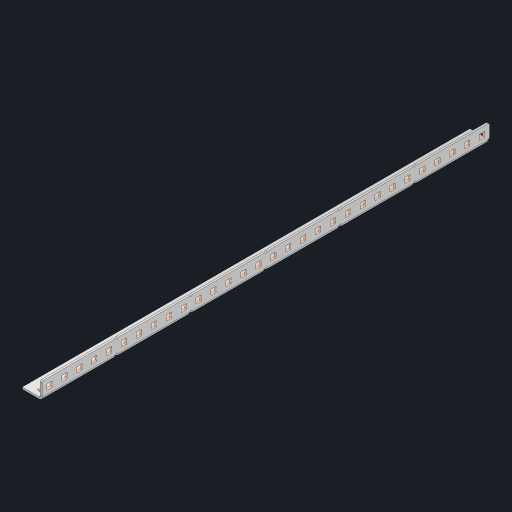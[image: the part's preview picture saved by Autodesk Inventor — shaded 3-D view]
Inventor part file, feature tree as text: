
AUTODESK INVENTOR PART (.ipt)
format: ipt  version: 2023 (Build 270158000, 158)  size: 974,848 bytes
history: native  units: in
note: dims shown in document units (in); Inventor stores cm internally (conversion verified against a paired STEP export)
features: other x65, extrude x59, sheet_metal_op x10, sketch x8, mirror x1, pattern_linear x1, chamfer x1
ambient origin geometry x8: Origin, YZ Plane, XZ Plane, XY Plane, X Axis, Y Axis, Z Axis, Center Point
bodies: Solid1 (feature_tree), Body (feature_tree)
feature tree (145):
  other  "Flange Pattern Plane"
  sheet_metal_op  "Flange Pattern"
  sheet_metal_op  "Body Pattern"
  other  "Arc Length"
  mirror  "Notch Mirror"
  pattern_linear  "Notch Pattern"  Spacing1=0.25in  [1 undecoded]
  chamfer  "End Chamfer"
  extrude  "Half Cut"  Depth=0.0625in
  sketch  "Sketch1"  dims[d0=1.5in]
  other  "Plate1"
  sketch  "Sketch2"  dims[d1=15.0in]
  other  "Plate2"
  sheet_metal_op  "Bend1"
  sheet_metal_op  "Corner1"
  sketch  "Sketch3"  dims[d2=0.0625in]
  other  "Flange Pattern Sketch"
  sketch  "Sketch7"  dims[d3=0.0625in]
  other  "Srf1"
  other  "Srf2"
  sketch  "Sketch8"  dims[d4=0.0312in]
  sketch  "Sketch9"  dims[d5=0.125in]
  other  "Srf91"
  sheet_metal_op  "Body Pattern Sketch"
  other  "Srf92"
  sketch  "Sketch13"  dims[d6=0.0625in]
  sketch  "Sketch14"  dims[d7=0.5in d8=90.0deg d9=0.0312in d10=0.25in d11=0.0625in d12=0.0625in d16=0.182in d17=0.02in d18=0.0625in d19=0.0in d20=0.25in d21=0.25in d46=0.172in d47=1.0in d48=0.0in d49=0.182in d50=0.02in d51=0.25in d52=0.25in d53=0.0625in d54=0.0in d55=0.172in d56=1.0in d57=0.0in d60=11.811in d62=0.5in d63=0.3937in d65=0.5in d85=0.1473in d86=0.1782in d88=0.04in d89=0.0625in d90=0.0in d91=0.04in d92=0.0491in d95=2.5in d96=0.04in d97=0.25in d98=45.0deg d101=0.0in d102=2.497in d131=0.5in d132=11.811in d134=0.5in d139=0.5in]
  other  "Srf856"
  other  "Srf1310"
  other  "Srf1311"
  other  "Srf1312"
  other  "Srf1376"
  other  "Srf1377"
  other  "Srf1728"
  other  "Srf1755"
  other  "Srf1878"
  other  "Srf1879"
  other  "Srf1880"
  other  "Srf1881"
  other  "Srf1882"
  other  "Srf1883"
  other  "Srf1884"
  other  "Srf1885"
  other  "Srf1886"
  other  "Srf1887"
  other  "Srf1888"
  other  "Srf1889"
  other  "Srf1890"
  other  "Srf1891"
  other  "Srf1892"
  other  "Srf1893"
  other  "Srf1894"
  other  "Srf1895"
  other  "Srf1896"
  other  "Srf1897"
  other  "Srf1898"
  other  "Srf1899"
  other  "Srf1900"
  other  "Srf1901"
  other  "Srf1942"
  other  "Srf1943"
  other  "Srf1944"
  other  "Srf1945"
  other  "Srf1946"
  other  "Srf1947"
  other  "Srf1948"
  other  "Srf1949"
  other  "Srf1950"
  other  "Srf1951"
  other  "Srf1952"
  other  "Srf1953"
  other  "Srf1954"
  other  "Srf1955"
  other  "Srf1956"
  other  "Srf1957"
  other  "Srf1958"
  other  "Srf1959"
  other  "Srf1960"
  other  "Srf1961"
  other  "Srf1962"
  other  "Srf1963"
  other  "Srf1964"
  other  "Srf1965"
  sheet_metal_op  "Flange Stamp"
  sheet_metal_op  "Flange Circle"
  sheet_metal_op  "Body Stamp"
  sheet_metal_op  "Body Circle"
  sheet_metal_op  "Notch"
  extrude  "ExtrusionSrf2"  Depth=0.0625in
  extrude  "ExtrusionSrf92"  Depth=0.0625in
  extrude  "ExtrusionSrf856"  Depth=0.02in
  extrude  "ExtrusionSrf1310"  Depth=0.0625in
  extrude  "ExtrusionSrf1311"  TaperAngle=0.0deg  [1 undecoded]
  extrude  "ExtrusionSrf1312"  Depth=0.0625in
  extrude  "ExtrusionSrf1376"  Depth=0.0625in
  extrude  "ExtrusionSrf1377"  Depth=0.0625in
  extrude  "ExtrusionSrf1728"  Depth=0.0625in TaperAngle=0.0deg
  extrude  "ExtrusionSrf1755"  Depth=0.0625in
  extrude  "ExtrusionSrf1878"  Depth=0.02in
  extrude  "ExtrusionSrf1879"  Depth=0.0625in
  extrude  "ExtrusionSrf1880"  Depth=0.0625in
  extrude  "ExtrusionSrf1881"  Depth=0.0625in
  extrude  "ExtrusionSrf1882"  TaperAngle=0.0deg  [1 undecoded]
  extrude  "ExtrusionSrf1883"  Depth=0.0625in
  extrude  "ExtrusionSrf1884"  Depth=0.0625in TaperAngle=0.0deg
  extrude  "ExtrusionSrf1885"  Depth=0.0625in
  extrude  "ExtrusionSrf1886"  Depth=0.3937in
  extrude  "ExtrusionSrf1887"  Depth=0.0625in
  extrude  "ExtrusionSrf1888"  Depth=0.0625in
  extrude  "ExtrusionSrf1889"  Depth=0.0625in
  extrude  "ExtrusionSrf1890"  Depth=0.0625in
  extrude  "ExtrusionSrf1891"  TaperAngle=0.0deg  [1 undecoded]
  extrude  "ExtrusionSrf1892"  Depth=0.0625in
  extrude  "ExtrusionSrf1893"  Depth=0.0625in
  extrude  "ExtrusionSrf1894"  Depth=0.0625in
  extrude  "ExtrusionSrf1895"  Depth=0.0625in TaperAngle=45.0deg
  extrude  "ExtrusionSrf1896"  TaperAngle=0.0deg  [1 undecoded]
  extrude  "ExtrusionSrf1897"  Depth=0.0625in
  extrude  "ExtrusionSrf1898"  Depth=0.0625in
  extrude  "ExtrusionSrf1899"  Depth=0.0625in
  extrude  "ExtrusionSrf1900"  Depth=0.0625in
  extrude  "ExtrusionSrf1901"  Depth=0.0625in
  extrude  "ExtrusionSrf1942"  [1 undecoded]
  extrude  "ExtrusionSrf1943"  [1 undecoded]
  extrude  "ExtrusionSrf1944"  [1 undecoded]
  extrude  "ExtrusionSrf1945"  [1 undecoded]
  extrude  "ExtrusionSrf1946"  [1 undecoded]
  extrude  "ExtrusionSrf1947"  [1 undecoded]
  extrude  "ExtrusionSrf1948"  [1 undecoded]
  extrude  "ExtrusionSrf1949"  [1 undecoded]
  extrude  "ExtrusionSrf1950"  [1 undecoded]
  extrude  "ExtrusionSrf1951"  [1 undecoded]
  extrude  "ExtrusionSrf1952"  [1 undecoded]
  extrude  "ExtrusionSrf1953"  [1 undecoded]
  extrude  "ExtrusionSrf1954"  [1 undecoded]
  extrude  "ExtrusionSrf1955"  [1 undecoded]
  extrude  "ExtrusionSrf1956"  [1 undecoded]
  extrude  "ExtrusionSrf1957"  [1 undecoded]
  extrude  "ExtrusionSrf1958"  [1 undecoded]
  extrude  "ExtrusionSrf1959"  [1 undecoded]
  extrude  "ExtrusionSrf1960"  [1 undecoded]
  extrude  "ExtrusionSrf1961"  [1 undecoded]
  extrude  "ExtrusionSrf1962"  [1 undecoded]
  extrude  "ExtrusionSrf1963"  [1 undecoded]
  extrude  "ExtrusionSrf1964"  [1 undecoded]
  extrude  "ExtrusionSrf1965"  [1 undecoded]
note: 29 required parameter values undecoded (feature->parameter linkage not recoverable at this tier; creation-order binding heuristic only, values carry confidence <= 0.55)
